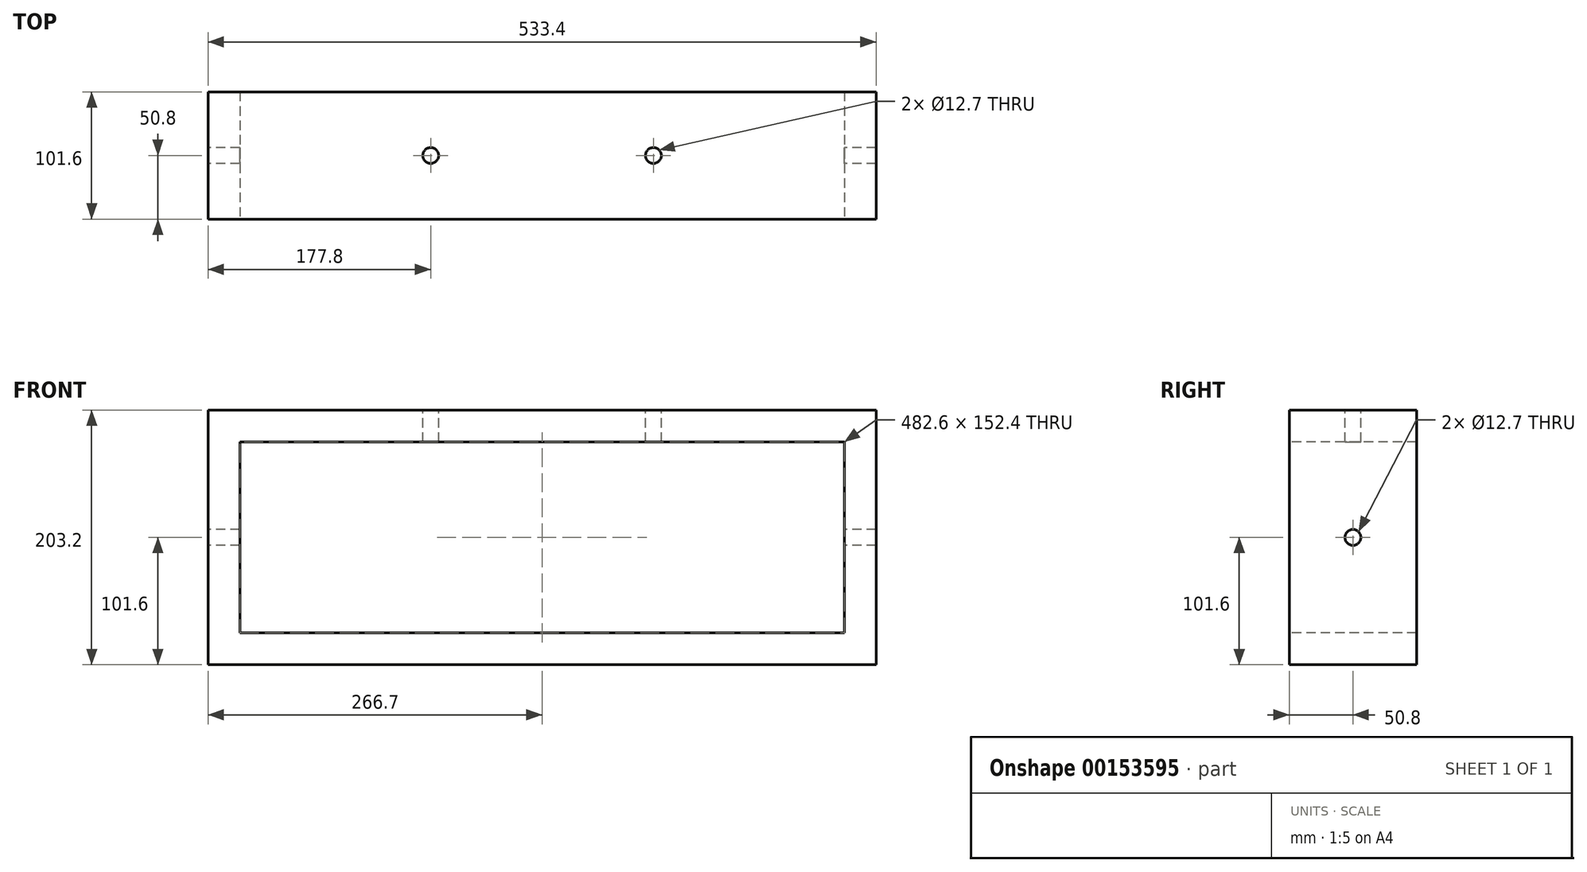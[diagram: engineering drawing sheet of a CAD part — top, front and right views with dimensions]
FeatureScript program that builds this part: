
annotation { "Feature Type Name" : "Feature", "Feature Type Description" : "" }
export const myFeature = defineFeature(function(context is Context, id is Id, definition is map)
    precondition{}
    {
        {
            var Q0;
            Q0=qCreatedBy(makeId("Front.planeOp"),FACE);
            var sketch = newSketch(context, id + "F0", { "sketchPlane" : qUnion([Q0])});
            skLineSegment(sketch, "E0.bottom", {"start": v(-266.7, 101.6) * mm, "end": v(266.7, 101.6) * mm});
            skLineSegment(sketch, "E0.top", {"start": v(-266.7, -101.6) * mm, "end": v(266.7, -101.6) * mm});
            skLineSegment(sketch, "E0.left", {"start": v(-266.7, 101.6) * mm, "end": v(-266.7, -101.6) * mm});
            skLineSegment(sketch, "E0.right", {"start": v(266.7, 101.6) * mm, "end": v(266.7, -101.6) * mm});
            skPoint(sketch, "E0.middle", {"position": v(0, 0) * mm});
            skLineSegment(sketch, "E1", {"start": v(-266.7, 101.6) * mm, "end": v(-266.7, 76.2) * mm});
            skLineSegment(sketch, "E2", {"start": v(-266.7, 76.2) * mm, "end": v(266.7, 76.2) * mm});
            skLineSegment(sketch, "E3", {"start": v(-266.7, 76.2) * mm, "end": v(-241.3, 76.2) * mm});
            skLineSegment(sketch, "E4", {"start": v(-241.3, 76.2) * mm, "end": v(-241.3, -101.6) * mm});
            skLineSegment(sketch, "E5", {"start": v(266.7, 76.2) * mm, "end": v(241.3, 76.2) * mm});
            skLineSegment(sketch, "E6", {"start": v(241.3, 76.2) * mm, "end": v(241.3, -101.6) * mm});
            skLineSegment(sketch, "E7", {"start": v(241.3, -101.6) * mm, "end": v(241.3, -76.2) * mm});
            skLineSegment(sketch, "E8", {"start": v(241.3, -76.2) * mm, "end": v(-241.3, -76.2) * mm});
            skLineSegment(sketch, "E9", {"start": v(-266.7, 76.2) * mm, "end": v(-266.7, -101.6) * mm});
            skSolve(sketch);
        }
        {
            var Q0;
            Q0=qSketchRegion(id+"F0",true);
            var Q1;
            Q1=makeQuery(id+"F0.imprint","IMPRINT",FACE,{"disambiguationData":[TD([[makeQuery(id+"F0.imprint","IMPRINT",EDGE,{"derivedFrom":sQuery(id+"F0.wireOp",EDGE,"E0.bottom")}),-1.0]])]});
            extrude(context, id + "F1", {"entities" : qUnion([Q0, Q1]), "oppositeDirection" : true, "depth" : 101.6 * mm});
        }
        {
            var Q0;
            Q0=makeQuery(id+"F1.opExtrude","CAP_FACE",FACE,{"disambiguationData":[OSD([sQuery(id+"F0.wireOp",EDGE,"E0.bottom"),sQuery(id+"F0.wireOp",EDGE,"E0.top"),sQuery(id+"F0.wireOp",EDGE,"E0.left"),sQuery(id+"F0.wireOp",EDGE,"E0.right")])],"isStart":true});
            var sketch = newSketch(context, id + "F2", { "sketchPlane" : qUnion([Q0])});
            skLineSegment(sketch, "E10.bottom", {"start": v(241.3, 76.2) * mm, "end": v(-241.3, 76.2) * mm});
            skLineSegment(sketch, "E10.top", {"start": v(241.3, -76.2) * mm, "end": v(-241.3, -76.2) * mm});
            skLineSegment(sketch, "E10.left", {"start": v(241.3, 76.2) * mm, "end": v(241.3, -76.2) * mm});
            skLineSegment(sketch, "E10.right", {"start": v(-241.3, 76.2) * mm, "end": v(-241.3, -76.2) * mm});
            skPoint(sketch, "E10.middle", {"position": v(0, 0) * mm});
            skSolve(sketch);
        }
        {
            var Q0;
            Q0=qSketchRegion(id+"F2",true);
            extrude(context, id + "F3", {"entities" : qUnion([Q0]), "operationType" : NewBodyOperationType.REMOVE, "oppositeDirection" : true, "depth" : 101.6 * mm});
        }
        {
            var Q0;
            Q0=qCreatedBy(makeId("Right.planeOp"),FACE);
            var sketch = newSketch(context, id + "F4", { "sketchPlane" : qUnion([Q0])});
            skLineSegment(sketch, "E11", {"start": v(50.8, 101.6) * mm, "end": v(50.8, -101.6) * mm, "construction": true});
            skLineSegment(sketch, "E12", {"start": v(0, 0) * mm, "end": v(101.6, 0) * mm, "construction": true});
            skPoint(sketch, "E13", {"position": v(50.8, 0) * mm});
            skCircle(sketch, "E14", {"center": v(50.8, 0) * mm, "radius": 6.35 * mm});
            skSolve(sketch);
        }
        {
            var Q0;
            Q0=makeQuery(id+"F4.imprint","IMPRINT",FACE,{"disambiguationData":[TD([[makeQuery(id+"F4.imprint","IMPRINT",EDGE,{"derivedFrom":sQuery(id+"F4.wireOp",EDGE,"E14")}),1.0]])]});
            var Q1;
            Q1=sQuery(id+"F4.wireOp",EDGE,"E14");
            extrude(context, id + "F5", {"entities" : qUnion([Q0]), "operationType" : NewBodyOperationType.REMOVE, "surfaceEntities" : qUnion([Q1]), "endBound" : BoundingType.THROUGH_ALL, "depth" : 25.4 * mm, "hasSecondDirection" : true, "secondDirectionBound" : SecondDirectionBoundingType.THROUGH_ALL, "secondDirectionOppositeDirection" : true, "secondDirectionDepth" : 25.4 * mm});
        }
        {
            var Q0;
            Q0=makeQuery(id+"F1.opExtrude","SWEPT_FACE",FACE,{"disambiguationData":[OSD([sQuery(id+"F0.wireOp",EDGE,"E0.bottom")])]});
            var sketch = newSketch(context, id + "F6", { "sketchPlane" : qUnion([Q0])});
            skLineSegment(sketch, "E15", {"start": v(-266.7, 50.8) * mm, "end": v(266.7, 50.8) * mm, "construction": true});
            skLineSegment(sketch, "E16", {"start": v(-266.7, 50.8) * mm, "end": v(-88.9, 50.8) * mm, "construction": true});
            skLineSegment(sketch, "E17", {"start": v(-88.9, 50.8) * mm, "end": v(88.9, 50.8) * mm, "construction": true});
            skLineSegment(sketch, "E18", {"start": v(88.9, 50.8) * mm, "end": v(266.7, 50.8) * mm, "construction": true});
            skLineSegment(sketch, "E19", {"start": v(-88.9, 101.6) * mm, "end": v(-88.9, 0) * mm, "construction": true});
            skLineSegment(sketch, "E20", {"start": v(88.9, 0) * mm, "end": v(88.9, 101.6) * mm, "construction": true});
            skCircle(sketch, "E21", {"center": v(-88.9, 50.8) * mm, "radius": 6.35 * mm});
            skCircle(sketch, "E22", {"center": v(88.9, 50.8) * mm, "radius": 6.35 * mm});
            skSolve(sketch);
        }
        {
            var Q0;
            Q0=qSketchRegion(id+"F6",true);
            extrude(context, id + "F7", {"entities" : qUnion([Q0]), "operationType" : NewBodyOperationType.REMOVE, "oppositeDirection" : true, "depth" : 25.4 * mm});
        }
    });
